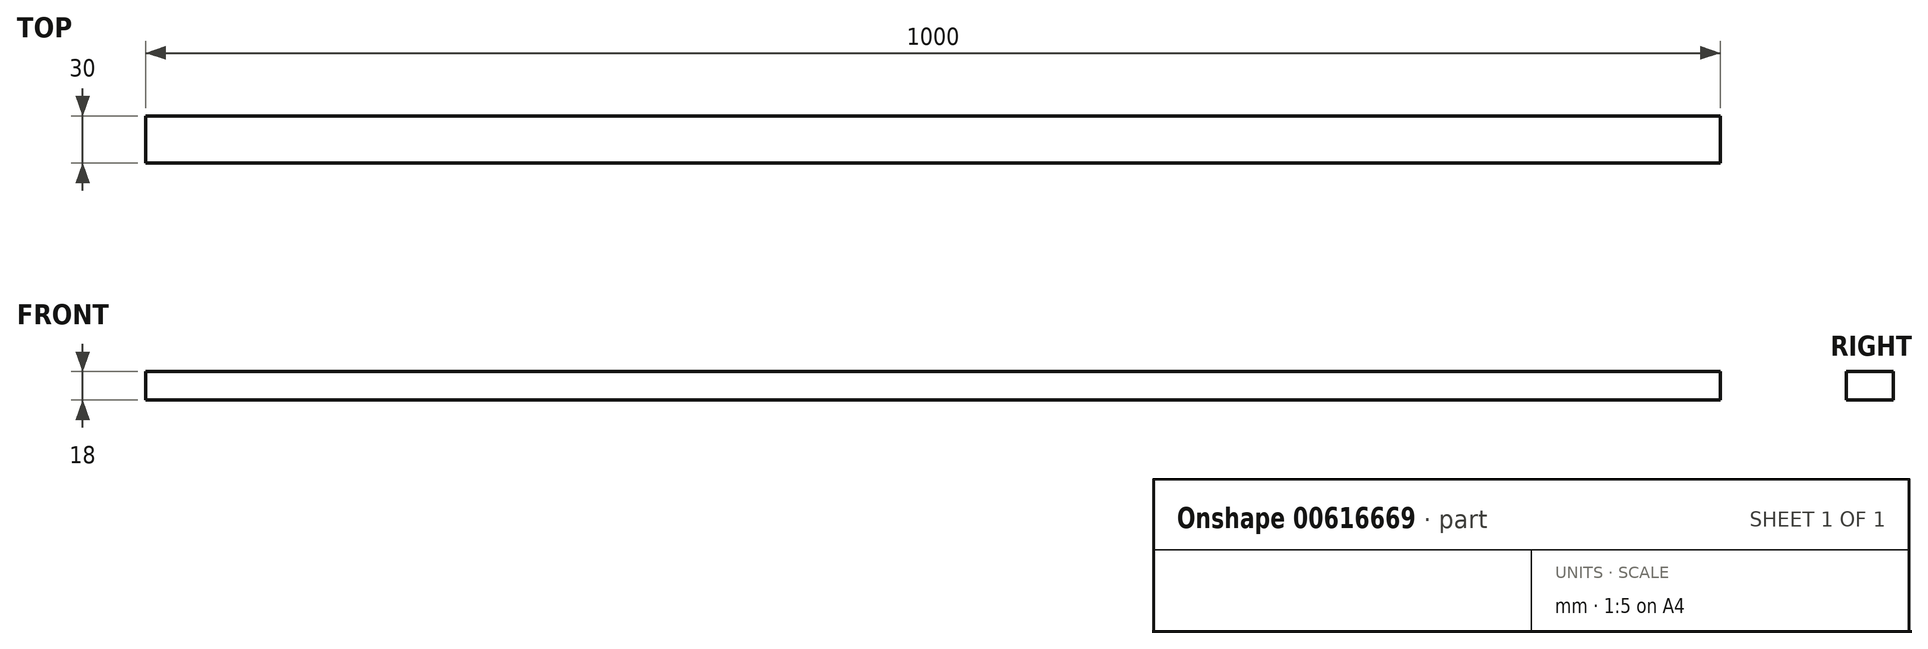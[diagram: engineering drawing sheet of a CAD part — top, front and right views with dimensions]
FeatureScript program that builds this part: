
annotation { "Feature Type Name" : "Feature", "Feature Type Description" : "" }
export const myFeature = defineFeature(function(context is Context, id is Id, definition is map)
    precondition{}
    {
        {
            var Q0;
            Q0=qCreatedBy(makeId("Top.planeOp"),FACE);
            var sketch = newSketch(context, id + "F0", { "sketchPlane" : qUnion([Q0])});
            skLineSegment(sketch, "E0.bottom", {"start": v(0, 0) * mm, "end": v(1000, 0) * mm});
            skLineSegment(sketch, "E0.top", {"start": v(0, 30) * mm, "end": v(1000, 30) * mm});
            skLineSegment(sketch, "E0.left", {"start": v(0, 0) * mm, "end": v(0, 30) * mm});
            skLineSegment(sketch, "E0.right", {"start": v(1000, 0) * mm, "end": v(1000, 30) * mm});
            skSolve(sketch);
        }
        {
            var Q0;
            Q0=makeQuery(id+"F0.imprint","IMPRINT",FACE,{"disambiguationData":[TD([[makeQuery(id+"F0.imprint","IMPRINT",EDGE,{"derivedFrom":sQuery(id+"F0.wireOp",EDGE,"E0.bottom")}),1.0]])]});
            extrude(context, id + "F1", {"entities" : qUnion([Q0]), "depth" : 18 * mm, "offsetDistance" : 25 * mm});
        }
    });
